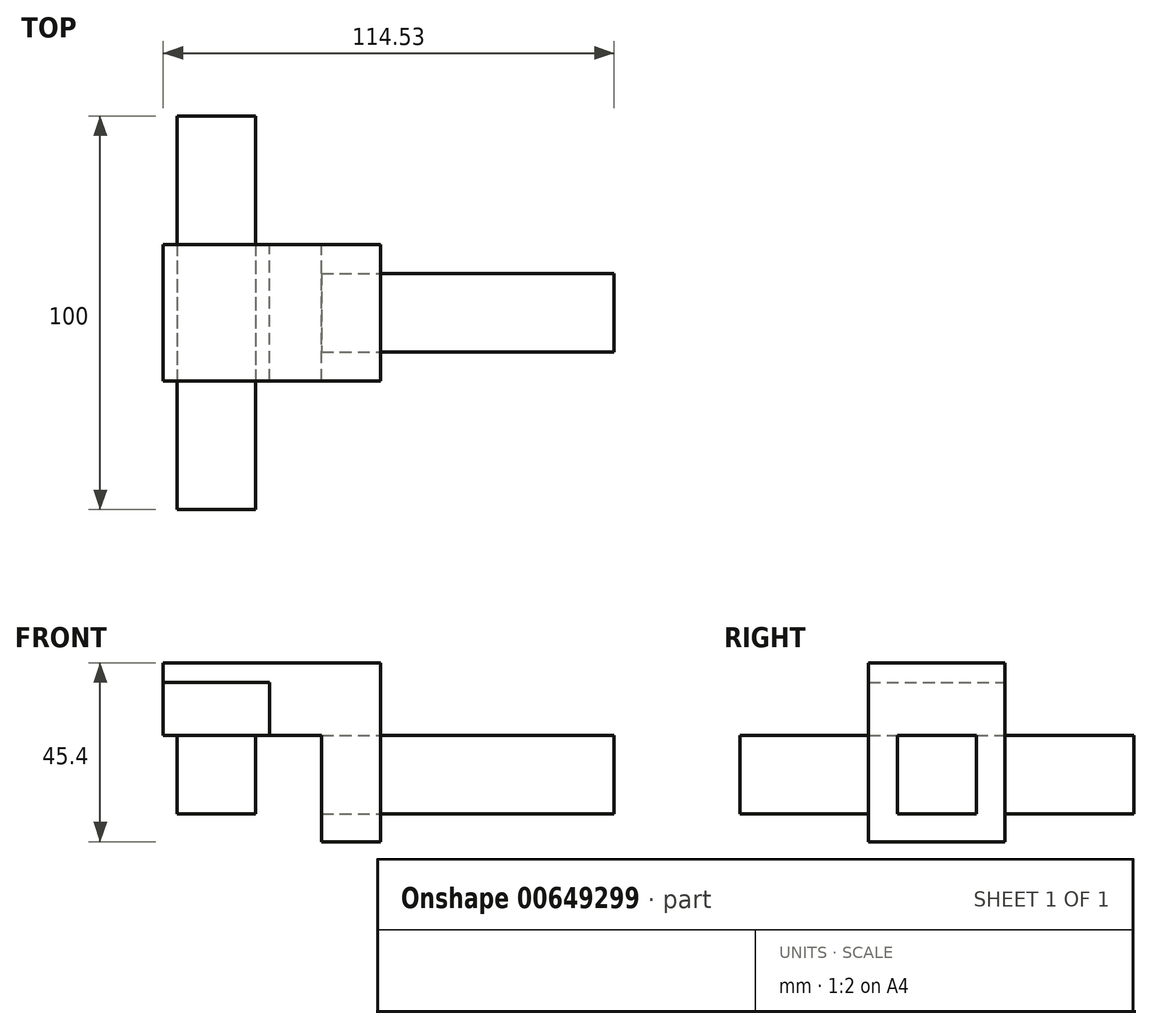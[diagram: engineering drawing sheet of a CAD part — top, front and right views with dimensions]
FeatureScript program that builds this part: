
annotation { "Feature Type Name" : "Feature", "Feature Type Description" : "" }
export const myFeature = defineFeature(function(context is Context, id is Id, definition is map)
    precondition{}
    {
        {
            var Q0;
            Q0=qCreatedBy(makeId("Top.planeOp"),FACE);
            var sketch = newSketch(context, id + "F0", { "sketchPlane" : qUnion([Q0])});
            skLineSegment(sketch, "E0.bottom", {"start": v(-43.8, 50) * mm, "end": v(-23.8, 50) * mm});
            skLineSegment(sketch, "E0.top", {"start": v(-43.8, -50) * mm, "end": v(-23.8, -50) * mm});
            skLineSegment(sketch, "E0.left", {"start": v(-43.8, 50) * mm, "end": v(-43.8, -50) * mm});
            skLineSegment(sketch, "E0.right", {"start": v(-23.8, 50) * mm, "end": v(-23.8, -50) * mm});
            skLineSegment(sketch, "E1.bottom", {"start": v(-7.06, 10) * mm, "end": v(67.23, 10) * mm});
            skLineSegment(sketch, "E1.top", {"start": v(-7.06, -10) * mm, "end": v(67.23, -10) * mm});
            skLineSegment(sketch, "E1.left", {"start": v(-7.06, 10) * mm, "end": v(-7.06, -10) * mm});
            skLineSegment(sketch, "E1.right", {"start": v(67.23, 10) * mm, "end": v(67.23, -10) * mm});
            skSolve(sketch);
        }
        {
            var Q0;
            Q0=makeQuery(id+"F0.imprint","IMPRINT",FACE,{"disambiguationData":[TD([[makeQuery(id+"F0.imprint","IMPRINT",EDGE,{"derivedFrom":sQuery(id+"F0.wireOp",EDGE,"E0.bottom")}),-1.0]])]});
            var Q1;
            Q1=makeQuery(id+"F0.imprint","IMPRINT",FACE,{"disambiguationData":[TD([[makeQuery(id+"F0.imprint","IMPRINT",EDGE,{"derivedFrom":sQuery(id+"F0.wireOp",EDGE,"E1.bottom")}),-1.0]])]});
            extrude(context, id + "F1", {"entities" : qUnion([Q0, Q1]), "depth" : 20 * mm, "offsetDistance" : 25 * mm});
        }
        {
            var Q0;
            Q0=makeQuery(id+"F1.opExtrude","CAP_FACE",FACE,{"disambiguationData":[OSD([sQuery(id+"F0.wireOp",EDGE,"E0.bottom"),sQuery(id+"F0.wireOp",EDGE,"E0.top"),sQuery(id+"F0.wireOp",EDGE,"E0.left"),sQuery(id+"F0.wireOp",EDGE,"E0.right")])],"isStart":false});
            var sketch = newSketch(context, id + "F2", { "sketchPlane" : qUnion([Q0])});
            skLineSegment(sketch, "E2.bottom", {"start": v(-47.3, 17.35) * mm, "end": v(-20.3, 17.35) * mm});
            skLineSegment(sketch, "E2.top", {"start": v(-47.3, -17.35) * mm, "end": v(-20.3, -17.35) * mm});
            skLineSegment(sketch, "E2.left", {"start": v(-47.3, 17.35) * mm, "end": v(-47.3, -17.35) * mm});
            skLineSegment(sketch, "E2.right", {"start": v(-20.3, 17.35) * mm, "end": v(-20.3, -17.35) * mm});
            skLineSegment(sketch, "E3", {"start": v(-33.8, 50) * mm, "end": v(-33.8, -50) * mm, "construction": true});
            skSolve(sketch);
        }
        {
            var Q0;
            {var subQ0=sQuery(id+"F2.wireOp",EDGE,"E2.left");Q0=makeQuery(id+"F2.imprint","IMPRINT",FACE,{"disambiguationData":[TD([[makeQuery(id+"F2.imprint","IMPRINT",EDGE,{"derivedFrom":subQ0}),1.0]])]});}
            var Q1;
            {var subQ0=sQuery(id+"F2.wireOp",EDGE,"E2.bottom");var subQ1=makeQuery(id+"F1.opExtrude","CAP_EDGE",EDGE,{"disambiguationData":[OSD([sQuery(id+"F0.wireOp",EDGE,"E0.left")])],"isStart":false});var subQ2=makeQuery(id+"F2.imprint","INTERSECT",VERTEX,{"derivedFrom":[subQ1,subQ0]});Q1=makeQuery(id+"F2.imprint","IMPRINT",FACE,{"disambiguationData":[TD([[makeQuery(id+"F2.imprint","IMPRINT",EDGE,{"disambiguationData":[TD([[subQ2,-1.0]])],"derivedFrom":subQ0}),-1.0]])]});}
            var Q2;
            {var subQ0=sQuery(id+"F2.wireOp",EDGE,"E2.right");Q2=makeQuery(id+"F2.imprint","IMPRINT",FACE,{"disambiguationData":[TD([[makeQuery(id+"F2.imprint","IMPRINT",EDGE,{"derivedFrom":subQ0}),-1.0]])]});}
            extrude(context, id + "F3", {"entities" : qUnion([Q0, Q1, Q2]), "depth" : 13.4 * mm, "offsetDistance" : 25 * mm});
        }
        {
            var Q0;
            Q0=qCreatedBy(makeId("Front.planeOp"),FACE);
            var sketch = newSketch(context, id + "F4", { "sketchPlane" : qUnion([Q0])});
            skLineSegment(sketch, "E4", {"start": v(-47.3, 38.4) * mm, "end": v(7.94, 38.4) * mm});
            skLineSegment(sketch, "E5", {"start": v(7.94, 38.4) * mm, "end": v(7.94, -7) * mm});
            skLineSegment(sketch, "E6", {"start": v(7.94, -7) * mm, "end": v(-7.06, -7) * mm});
            skLineSegment(sketch, "E7", {"start": v(-7.06, -7) * mm, "end": v(-7.06, 20) * mm});
            skLineSegment(sketch, "E8", {"start": v(-7.06, 20) * mm, "end": v(-20.3, 20) * mm});
            skLineSegment(sketch, "E9", {"start": v(-20.3, 20) * mm, "end": v(-20.3, 33.4) * mm});
            skLineSegment(sketch, "E10", {"start": v(-20.3, 33.4) * mm, "end": v(-47.3, 33.4) * mm});
            skLineSegment(sketch, "E11", {"start": v(-47.3, 33.4) * mm, "end": v(-47.3, 38.4) * mm});
            skSolve(sketch);
        }
        {
            var Q0;
            Q0=makeQuery(id+"F4.imprint","IMPRINT",FACE,{"disambiguationData":[TD([[makeQuery(id+"F4.imprint","IMPRINT",EDGE,{"derivedFrom":sQuery(id+"F4.wireOp",EDGE,"E4")}),-1.0]])]});
            var Q1;
            Q1=makeQuery(id+"F3.opExtrude","SWEPT_FACE",FACE,{"disambiguationData":[OSD([sQuery(id+"F2.wireOp",EDGE,"E2.top")])]});
            var Q2;
            Q2=makeQuery(id+"F3.opExtrude","SWEPT_FACE",FACE,{"disambiguationData":[OSD([sQuery(id+"F2.wireOp",EDGE,"E2.bottom")])]});
            extrude(context, id + "F5", {"entities" : qUnion([Q0]), "endBound" : BoundingType.UP_TO_SURFACE, "depth" : 25 * mm, "endBoundEntityFace" : qUnion([Q1]), "offsetDistance" : 25 * mm, "hasSecondDirection" : true, "secondDirectionBound" : SecondDirectionBoundingType.UP_TO_SURFACE, "secondDirectionOppositeDirection" : true, "secondDirectionDepth" : 25 * mm, "secondDirectionBoundEntityFace" : qUnion([Q2])});
        }
        {
            var Q0;
            Q0=makeQuery(id+"F1.opExtrude","SWEPT_BODY",BODY,{"disambiguationData":[OSD([sQuery(id+"F0.wireOp",EDGE,"E1.bottom"),sQuery(id+"F0.wireOp",EDGE,"E1.top"),sQuery(id+"F0.wireOp",EDGE,"E1.left"),sQuery(id+"F0.wireOp",EDGE,"E1.right")])]});
            var Q1;
            Q1=makeQuery(id+"F5.opExtrude","SWEPT_BODY",BODY,{"disambiguationData":[OSD([sQuery(id+"F4.wireOp",EDGE,"E4"),sQuery(id+"F4.wireOp",EDGE,"E5"),sQuery(id+"F4.wireOp",EDGE,"E6"),sQuery(id+"F4.wireOp",EDGE,"E7"),sQuery(id+"F4.wireOp",EDGE,"E8"),sQuery(id+"F4.wireOp",EDGE,"E9"),sQuery(id+"F4.wireOp",EDGE,"E10"),sQuery(id+"F4.wireOp",EDGE,"E11")])]});
            booleanBodies(context, id + "F6", {"operationType" : BooleanOperationType.SUBTRACTION, "tools" : qUnion([Q0]), "targets" : qUnion([Q1]), "keepTools" : true});
        }
    });
